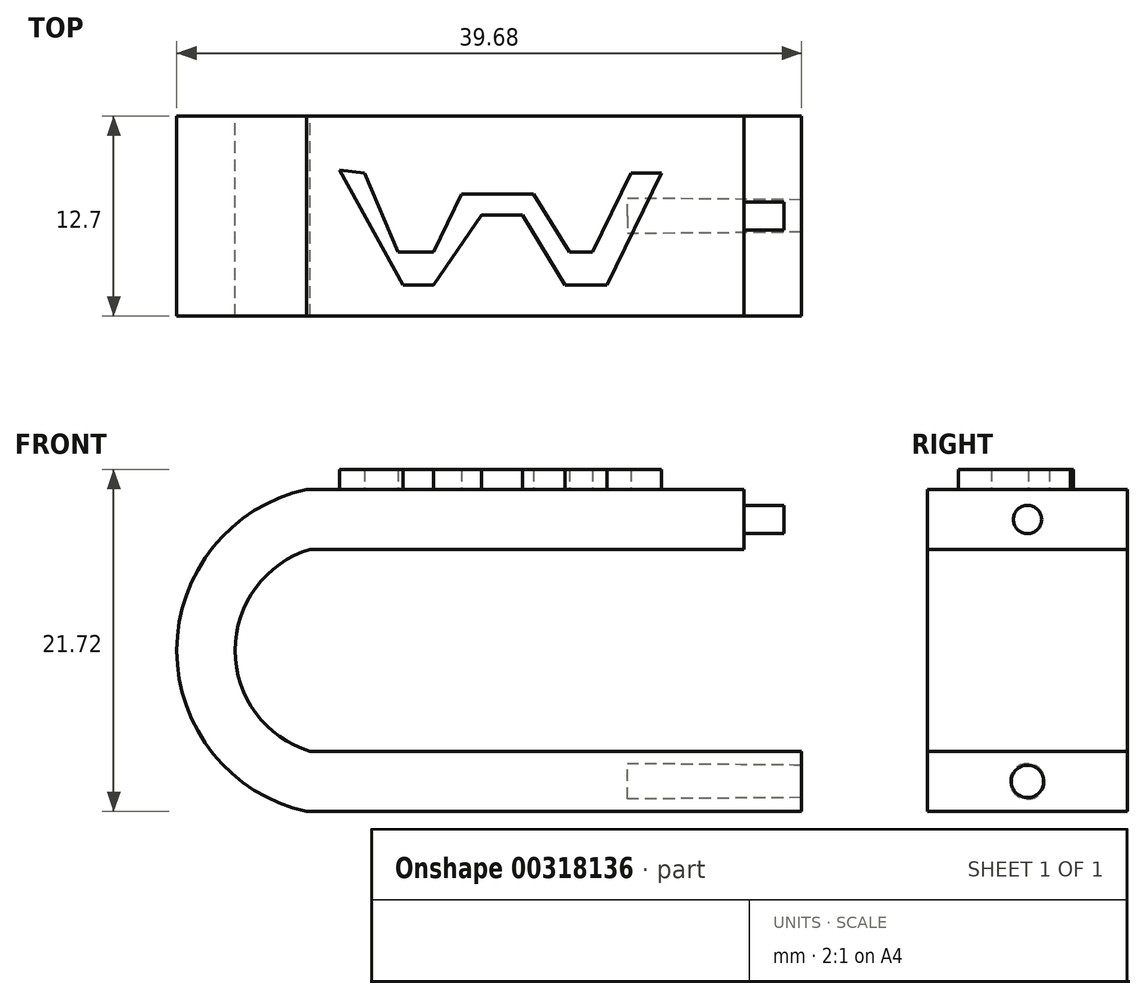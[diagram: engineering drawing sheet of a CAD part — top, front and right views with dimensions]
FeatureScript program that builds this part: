
annotation { "Feature Type Name" : "Feature", "Feature Type Description" : "" }
export const myFeature = defineFeature(function(context is Context, id is Id, definition is map)
    precondition{}
    {
        {
            var Q0;
            Q0=qCreatedBy(makeId("Front.planeOp"),FACE);
            var sketch = newSketch(context, id + "F0", { "sketchPlane" : qUnion([Q0])});
            skArc(sketch, "E0", {"start": v(-45.55, -18.21) * mm, "mid": v(-50.31, -24.63) * mm, "end": v(-45.55, -31.05) * mm});
            skArc(sketch, "E1", {"start": v(-45.79, -14.4) * mm, "mid": v(-54.02, -24.63) * mm, "end": v(-45.79, -34.86) * mm});
            skLineSegment(sketch, "E2", {"start": v(-45.79, -34.86) * mm, "end": v(-14.34, -34.86) * mm});
            skLineSegment(sketch, "E3", {"start": v(-14.34, -34.86) * mm, "end": v(-14.34, -31.05) * mm});
            skLineSegment(sketch, "E4", {"start": v(-14.34, -31.05) * mm, "end": v(-45.55, -31.05) * mm});
            skLineSegment(sketch, "E5", {"start": v(-45.55, -18.21) * mm, "end": v(-18, -18.21) * mm});
            skLineSegment(sketch, "E6", {"start": v(-18, -18.21) * mm, "end": v(-18, -14.4) * mm});
            skLineSegment(sketch, "E7", {"start": v(-18, -14.4) * mm, "end": v(-45.79, -14.4) * mm});
            skLineSegment(sketch, "E8", {"start": v(-45.79, -14.4) * mm, "end": v(-45.55, -18.21) * mm});
            skLineSegment(sketch, "E9", {"start": v(-45.79, -34.86) * mm, "end": v(-45.55, -31.05) * mm});
            skSolve(sketch);
        }
        {
            var Q0;
            Q0 = qSketchRegion(id + "F0", true);
            extrude(context, id + "F1", {"entities" : qUnion([Q0]), "depth" : 12.7 * mm});
        }
        {
            var Q0;
            Q0=makeQuery(id+"F1.opExtrude","SWEPT_FACE",FACE,{"disambiguationData":[OSD([sQuery(id+"F0.wireOp",EDGE,"E6")])]});
            var sketch = newSketch(context, id + "F2", { "sketchPlane" : qUnion([Q0])});
            skCircle(sketch, "E10", {"center": v(-6.34, -16.31) * mm, "radius": 0.9 * mm});
            skSolve(sketch);
        }
        {
            var Q0;
            Q0 = qSketchRegion(id + "F2", true);
            extrude(context, id + "F3", {"entities" : qUnion([Q0]), "operationType" : NewBodyOperationType.ADD, "depth" : 2.54 * mm});
        }
        {
            var Q0;
            Q0=qCreatedBy(makeId("Right.planeOp"),FACE);
            var sketch = newSketch(context, id + "F4", { "sketchPlane" : qUnion([Q0])});
            skCircle(sketch, "E11", {"center": v(-6.35, -32.95) * mm, "radius": 0.9 * mm});
            skSolve(sketch);
        }
        {
            var Q0;
            Q0 = qSketchRegion(id + "F4", true);
            extrude(context, id + "F5", {"entities" : qUnion([Q0]), "operationType" : NewBodyOperationType.REMOVE, "oppositeDirection" : true, "depth" : 25.4 * mm, "hasDraft" : true, "draftAngle" : .5 * degree});
        }
        {
            var Q0;
            Q0=makeQuery(id+"F1.opExtrude","SWEPT_FACE",FACE,{"disambiguationData":[OSD([sQuery(id+"F0.wireOp",EDGE,"E7")])]});
            var sketch = newSketch(context, id + "F6", { "sketchPlane" : qUnion([Q0])});
            skLineSegment(sketch, "E12", {"start": v(-43.7, -3.43) * mm, "end": v(-39.64, -10.73) * mm});
            skLineSegment(sketch, "E13", {"start": v(-39.64, -10.73) * mm, "end": v(-37.72, -10.73) * mm});
            skLineSegment(sketch, "E14", {"start": v(-37.72, -10.73) * mm, "end": v(-34.67, -6.28) * mm});
            skLineSegment(sketch, "E15", {"start": v(-34.67, -6.28) * mm, "end": v(-32.08, -6.28) * mm});
            skLineSegment(sketch, "E16", {"start": v(-32.08, -6.28) * mm, "end": v(-29.35, -10.73) * mm});
            skLineSegment(sketch, "E17", {"start": v(-29.35, -10.73) * mm, "end": v(-26.7, -10.73) * mm});
            skLineSegment(sketch, "E18", {"start": v(-26.7, -10.73) * mm, "end": v(-23.25, -3.63) * mm});
            skLineSegment(sketch, "E19", {"start": v(-25.17, -3.63) * mm, "end": v(-27.61, -8.65) * mm});
            skLineSegment(sketch, "E20", {"start": v(-27.61, -8.65) * mm, "end": v(-29.09, -8.65) * mm});
            skLineSegment(sketch, "E21", {"start": v(-29.09, -8.65) * mm, "end": v(-31.35, -4.95) * mm});
            skLineSegment(sketch, "E22", {"start": v(-31.35, -4.95) * mm, "end": v(-35.93, -4.95) * mm});
            skLineSegment(sketch, "E23", {"start": v(-35.93, -4.95) * mm, "end": v(-37.73, -8.65) * mm});
            skLineSegment(sketch, "E24", {"start": v(-37.73, -8.65) * mm, "end": v(-39.98, -8.65) * mm});
            skLineSegment(sketch, "E25", {"start": v(-39.98, -8.65) * mm, "end": v(-42.1, -3.63) * mm});
            skLineSegment(sketch, "E26", {"start": v(-42.1, -3.63) * mm, "end": v(-43.7, -3.43) * mm});
            skLineSegment(sketch, "E27", {"start": v(-25.17, -3.63) * mm, "end": v(-23.25, -3.63) * mm});
            skSolve(sketch);
        }
        {
            var Q0;
            Q0 = qSketchRegion(id + "F6", true);
            extrude(context, id + "F7", {"entities" : qUnion([Q0]), "operationType" : NewBodyOperationType.ADD, "depth" : 1.27 * mm});
        }
    });
